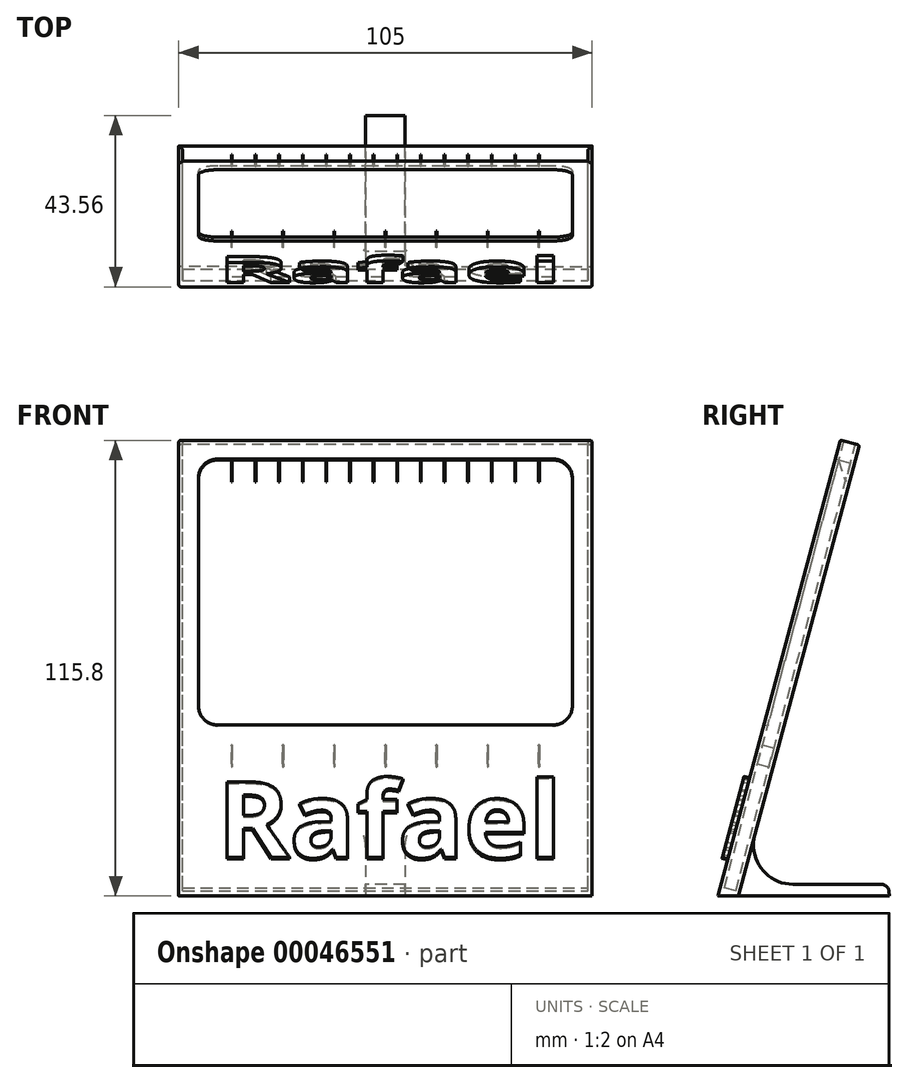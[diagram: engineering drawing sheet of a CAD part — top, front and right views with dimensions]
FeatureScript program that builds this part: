
annotation { "Feature Type Name" : "Feature", "Feature Type Description" : "" }
export const myFeature = defineFeature(function(context is Context, id is Id, definition is map)
    precondition{}
    {
        {
            var Q0;
            Q0=qCreatedBy(makeId("Right.planeOp"),FACE);
            var sketch = newSketch(context, id + "F0", { "sketchPlane" : qUnion([Q0])});
            skLineSegment(sketch, "E0", {"start": v(-21.78, 0) * mm, "end": v(9.28, 115.91) * mm});
            skLineSegment(sketch, "E1", {"start": v(9.28, 115.91) * mm, "end": v(14.1, 114.62) * mm});
            skLineSegment(sketch, "E2", {"start": v(14.1, 114.62) * mm, "end": v(-12.43, 15.59) * mm});
            skLineSegment(sketch, "E3", {"start": v(-2.77, 3) * mm, "end": v(19.68, 3) * mm});
            skLineSegment(sketch, "E4", {"start": v(21.68, 1.17) * mm, "end": v(21.78, 0) * mm});
            skLineSegment(sketch, "E5", {"start": v(21.78, 0) * mm, "end": v(-21.78, 0) * mm});
            skPoint(sketch, "E6.visualSharp", {"position": v(-15.8, 3) * mm});
            skArc(sketch, "E6.filletArc", {"start": v(-12.43, 15.59) * mm, "mid": v(-10.7, 6.91) * mm, "end": v(-2.77, 3) * mm});
            skLineSegment(sketch, "E7", {"start": v(21.52, 3) * mm, "end": v(11.7, 115.26) * mm, "construction": true});
            skPoint(sketch, "E7.endSnap0", {"position": v(11.7, 115.26) * mm});
            skPoint(sketch, "E8.visualSharp", {"position": v(21.52, 3) * mm});
            skArc(sketch, "E8.filletArc", {"start": v(21.68, 1.17) * mm, "mid": v(21.03, 2.47) * mm, "end": v(19.68, 3) * mm});
            skSolve(sketch);
        }
        {
            var Q0;
            Q0=makeQuery(id+"F0.imprint","IMPRINT",FACE,{"disambiguationData":[TD([[makeQuery(id+"F0.imprint","IMPRINT",EDGE,{"derivedFrom":sQuery(id+"F0.wireOp",EDGE,"E0")}),-1.0]])]});
            extrude(context, id + "F1", {"entities" : qUnion([Q0]), "depth" : 105 * mm});
        }
        {
            var Q0;
            Q0=makeQuery(id+"F1.opExtrude","SWEPT_FACE",FACE,{"disambiguationData":[OSD([sQuery(id+"F0.wireOp",EDGE,"E0")])]});
            var sketch = newSketch(context, id + "F2", { "sketchPlane" : qUnion([Q0])});
            skLineSegment(sketch, "E9.bottom", {"start": v(10, 109.36) * mm, "end": v(95, 109.36) * mm});
            skLineSegment(sketch, "E9.top", {"start": v(10, 39.36) * mm, "end": v(95, 39.36) * mm});
            skLineSegment(sketch, "E9.left", {"start": v(5, 104.36) * mm, "end": v(5, 44.36) * mm});
            skLineSegment(sketch, "E9.right", {"start": v(100, 104.36) * mm, "end": v(100, 44.36) * mm});
            skLineSegment(sketch, "E10", {"start": v(0, 54.36) * mm, "end": v(5, 54.36) * mm, "construction": true});
            skLineSegment(sketch, "E11", {"start": v(105, 54.36) * mm, "end": v(100, 54.36) * mm, "construction": true});
            skLineSegment(sketch, "E12", {"start": v(52.5, 109.36) * mm, "end": v(52.5, 114.36) * mm, "construction": true});
            skPoint(sketch, "E13.visualSharp", {"position": v(5, 109.36) * mm});
            skArc(sketch, "E13.filletArc", {"start": v(10, 109.36) * mm, "mid": v(6.46, 107.9) * mm, "end": v(5, 104.36) * mm});
            skPoint(sketch, "E14.visualSharp", {"position": v(100, 109.36) * mm});
            skArc(sketch, "E14.filletArc", {"start": v(100, 104.36) * mm, "mid": v(98.54, 107.9) * mm, "end": v(95, 109.36) * mm});
            skPoint(sketch, "E15.visualSharp", {"position": v(100, 39.36) * mm});
            skArc(sketch, "E15.filletArc", {"start": v(95, 39.36) * mm, "mid": v(98.54, 40.83) * mm, "end": v(100, 44.36) * mm});
            skPoint(sketch, "E16.visualSharp", {"position": v(5, 39.36) * mm});
            skArc(sketch, "E16.filletArc", {"start": v(5, 44.36) * mm, "mid": v(6.46, 40.83) * mm, "end": v(10, 39.36) * mm});
            skSolve(sketch);
        }
        {
            var Q0;
            Q0 = qSketchRegion(id + "F2", true);
            extrude(context, id + "F3", {"entities" : qUnion([Q0]), "operationType" : NewBodyOperationType.REMOVE, "oppositeDirection" : true, "depth" : 3.5 * mm});
        }
        {
            var Q0;
            Q0=makeQuery(id+"F1.opExtrude","SWEPT_FACE",FACE,{"disambiguationData":[OSD([sQuery(id+"F0.wireOp",EDGE,"E1")])]});
            var sketch = newSketch(context, id + "F4", { "sketchPlane" : qUnion([Q0])});
            skLineSegment(sketch, "E17.bottom", {"start": v(1, -17.04) * mm, "end": v(104, -17.04) * mm});
            skLineSegment(sketch, "E17.top", {"start": v(1, -20.04) * mm, "end": v(104, -20.04) * mm});
            skLineSegment(sketch, "E17.left", {"start": v(1, -17.04) * mm, "end": v(1, -20.04) * mm});
            skLineSegment(sketch, "E17.right", {"start": v(104, -17.04) * mm, "end": v(104, -20.04) * mm});
            skLineSegment(sketch, "E18", {"start": v(52.5, -21.04) * mm, "end": v(52.5, -20.04) * mm, "construction": true});
            skSolve(sketch);
        }
        {
            var Q0;
            Q0 = qSketchRegion(id + "F4", true);
            var Q1;
            Q1=makeQuery(id+"F1.opExtrude","SWEPT_FACE",FACE,{"disambiguationData":[OSD([sQuery(id+"F0.wireOp",EDGE,"E5")])]});
            extrude(context, id + "F5", {"entities" : qUnion([Q0]), "operationType" : NewBodyOperationType.REMOVE, "oppositeDirection" : true, "endBoundEntityFace" : qUnion([Q1]), "depth" : 117.5 * mm});
        }
        {
            var Q0;
            Q0=makeQuery(id+"F1.opExtrude","SWEPT_FACE",FACE,{"disambiguationData":[OSD([sQuery(id+"F0.wireOp",EDGE,"E0")])]});
            var sketch = newSketch(context, id + "F6", { "sketchPlane" : qUnion([Q0])});
            skText(sketch, "E19", { "text": "Rafael", "fontName": "OpenSans-Bold.ttf"});
            skLineSegment(sketch, "E20", {"start": v(52.5, 26.86) * mm, "end": v(52.5, 39.36) * mm, "construction": true});
            skLineSegment(sketch, "E21", {"start": v(52.5, 6.86) * mm, "end": v(52.5, -5.64) * mm, "construction": true});
            const initialGuessF6  = {"E19": [0.00982, 0.00417, 1, 0, 0.02]};
            skSetInitialGuess(sketch, initialGuessF6);
            skSolve(sketch);
        }
        {
            var Q0;
            Q0 = qSketchRegion(id + "F6", true);
            extrude(context, id + "F7", {"entities" : qUnion([Q0]), "operationType" : NewBodyOperationType.ADD, "depth" : 1.5 * mm});
        }
        {
            var Q0;
            Q0=makeQuery(id+"F1.opExtrude","CAP_FACE",FACE,{"disambiguationData":[OSD([sQuery(id+"F0.wireOp",EDGE,"E0"),sQuery(id+"F0.wireOp",EDGE,"E1"),sQuery(id+"F0.wireOp",EDGE,"E2"),sQuery(id+"F0.wireOp",EDGE,"E3"),sQuery(id+"F0.wireOp",EDGE,"E4"),sQuery(id+"F0.wireOp",EDGE,"E5"),sQuery(id+"F0.wireOp",EDGE,"E6.filletArc"),sQuery(id+"F0.wireOp",EDGE,"E8.filletArc")])],"isStart":false});
            var sketch = newSketch(context, id + "F8", { "sketchPlane" : qUnion([Q0])});
            skLineSegment(sketch, "E22", {"start": v(-12.43, 15.59) * mm, "end": v(-16.6, 0) * mm});
            skLineSegment(sketch, "E23", {"start": v(-16.6, 0) * mm, "end": v(21.78, 0) * mm});
            skArc(sketch, "E24.0", {"start": v(-12.43, 15.59) * mm, "mid": v(-10.7, 6.91) * mm, "end": v(-2.77, 3) * mm});
            skLineSegment(sketch, "E25.0", {"start": v(-2.77, 3) * mm, "end": v(19.68, 3) * mm});
            skArc(sketch, "E26.0", {"start": v(21.68, 1.17) * mm, "mid": v(21.03, 2.47) * mm, "end": v(19.68, 3) * mm});
            skLineSegment(sketch, "E27.0", {"start": v(21.68, 1.17) * mm, "end": v(21.78, 0) * mm});
            skSolve(sketch);
        }
        {
            var Q0;
            Q0 = qSketchRegion(id + "F8", true);
            extrude(context, id + "F9", {"entities" : qUnion([Q0]), "operationType" : NewBodyOperationType.REMOVE, "oppositeDirection" : true, "depth" : 47.5 * mm});
        }
        {
            var Q0;
            Q0=makeQuery(id+"F1.opExtrude","CAP_FACE",FACE,{"disambiguationData":[OSD([sQuery(id+"F0.wireOp",EDGE,"E0"),sQuery(id+"F0.wireOp",EDGE,"E1"),sQuery(id+"F0.wireOp",EDGE,"E2"),sQuery(id+"F0.wireOp",EDGE,"E3"),sQuery(id+"F0.wireOp",EDGE,"E4"),sQuery(id+"F0.wireOp",EDGE,"E5"),sQuery(id+"F0.wireOp",EDGE,"E6.filletArc"),sQuery(id+"F0.wireOp",EDGE,"E8.filletArc")])],"isStart":true});
            var sketch = newSketch(context, id + "F10", { "sketchPlane" : qUnion([Q0])});
            skLineSegment(sketch, "E28", {"start": v(12.43, 15.59) * mm, "end": v(16.6, 0) * mm});
            skLineSegment(sketch, "E29", {"start": v(16.6, 0) * mm, "end": v(-21.78, 0) * mm});
            skArc(sketch, "E30.0", {"start": v(12.43, 15.59) * mm, "mid": v(10.7, 6.91) * mm, "end": v(2.77, 3) * mm});
            skLineSegment(sketch, "E31.0", {"start": v(2.77, 3) * mm, "end": v(-19.68, 3) * mm});
            skArc(sketch, "E32.0", {"start": v(-21.68, 1.17) * mm, "mid": v(-21.03, 2.47) * mm, "end": v(-19.68, 3) * mm});
            skLineSegment(sketch, "E33.0", {"start": v(-21.68, 1.17) * mm, "end": v(-21.78, 0) * mm});
            skSolve(sketch);
        }
        {
            var Q0;
            Q0 = qSketchRegion(id + "F10", true);
            extrude(context, id + "F11", {"entities" : qUnion([Q0]), "operationType" : NewBodyOperationType.REMOVE, "oppositeDirection" : true, "depth" : 47.5 * mm});
        }
        {
            var Q0;
            Q0=makeQuery(id+"F1.opExtrude","CAP_EDGE",EDGE,{"disambiguationData":[OSD([sQuery(id+"F0.wireOp",EDGE,"E0")])],"isStart":false});
            var Q1;
            Q1=makeQuery(id+"F1.opExtrude","CAP_EDGE",EDGE,{"disambiguationData":[OSD([sQuery(id+"F0.wireOp",EDGE,"E2")])],"isStart":false});
            var Q2;
            Q2=makeQuery(id+"F1.opExtrude","CAP_EDGE",EDGE,{"disambiguationData":[OSD([sQuery(id+"F0.wireOp",EDGE,"E6.filletArc")])],"isStart":false});
            var Q3;
            Q3=makeQuery(id+"F1.opExtrude","CAP_EDGE",EDGE,{"disambiguationData":[OSD([sQuery(id+"F0.wireOp",EDGE,"E2")])],"isStart":true});
            var Q4;
            Q4=makeQuery(id+"F1.opExtrude","CAP_EDGE",EDGE,{"disambiguationData":[OSD([sQuery(id+"F0.wireOp",EDGE,"E0")])],"isStart":true});
            var Q5;
            Q5=makeQuery(id+"F1.opExtrude","SWEPT_FACE",FACE,{"disambiguationData":[OSD([sQuery(id+"F0.wireOp",EDGE,"E1")])]});
            var Q6;
            Q6=makeQuery(id+"F3.boolean.opBoolean","COPY",EDGE,{"derivedFrom":makeQuery(id+"F3.opExtrude","CAP_EDGE",EDGE,{"disambiguationData":[OSD([sQuery(id+"F2.wireOp",EDGE,"E9.top")])],"isStart":true})});
            var Q7;
            Q7=makeQuery(id+"F3.boolean.opBoolean","COPY",EDGE,{"derivedFrom":makeQuery(id+"F3.opExtrude","CAP_EDGE",EDGE,{"disambiguationData":[OSD([sQuery(id+"F2.wireOp",EDGE,"E16.filletArc")])],"isStart":true})});
            var Q8;
            Q8=makeQuery(id+"F3.boolean.opBoolean","COPY",EDGE,{"derivedFrom":makeQuery(id+"F3.opExtrude","CAP_EDGE",EDGE,{"disambiguationData":[OSD([sQuery(id+"F2.wireOp",EDGE,"E9.left")])],"isStart":true})});
            var Q9;
            Q9=makeQuery(id+"F11.boolean.opBoolean","COPY",EDGE,{"derivedFrom":makeQuery(id+"F11.opExtrude","CAP_EDGE",EDGE,{"disambiguationData":[OSD([sQuery(id+"F10.wireOp",EDGE,"E28")])],"isStart":false})});
            var Q10;
            Q10=makeQuery(id+"F11.boolean.opBoolean","COPY",EDGE,{"derivedFrom":makeQuery(id+"F11.opExtrude","CAP_EDGE",EDGE,{"disambiguationData":[OSD([sQuery(id+"F10.wireOp",EDGE,"E30.0")])],"isStart":false})});
            var Q11;
            Q11=makeQuery(id+"F9.boolean.opBoolean","COPY",EDGE,{"derivedFrom":makeQuery(id+"F9.opExtrude","CAP_EDGE",EDGE,{"disambiguationData":[OSD([sQuery(id+"F8.wireOp",EDGE,"E22")])],"isStart":false})});
            var Q12;
            Q12=makeQuery(id+"F9.boolean.opBoolean","COPY",EDGE,{"derivedFrom":makeQuery(id+"F9.opExtrude","CAP_EDGE",EDGE,{"disambiguationData":[OSD([sQuery(id+"F8.wireOp",EDGE,"E24.0")])],"isStart":false})});
            fillet(context, id + "F12", {"entities" : qUnion([Q0, Q1, Q2, Q3, Q4, Q5, Q6, Q7, Q8, Q9, Q10, Q11, Q12]), "radius" : .5 * mm, "tangentPropagation" : true, "allowEdgeOverflow" : false});
        }
        {
            var Q0;
            Q0=makeQuery(id+"F5.boolean.opBoolean","COPY",FACE,{"derivedFrom":makeQuery(id+"F5.opExtrude","SWEPT_FACE",FACE,{"disambiguationData":[OSD([sQuery(id+"F4.wireOp",EDGE,"E17.bottom")])]})});
            var sketch = newSketch(context, id + "F13", { "sketchPlane" : qUnion([Q0])});
            skLineSegment(sketch, "E34.bottom", {"start": v(13.4, 109.36) * mm, "end": v(13.6, 109.36) * mm});
            skLineSegment(sketch, "E34.top", {"start": v(13.4, 104.36) * mm, "end": v(13.6, 104.36) * mm});
            skLineSegment(sketch, "E34.left", {"start": v(13.4, 109.36) * mm, "end": v(13.4, 104.36) * mm});
            skLineSegment(sketch, "E34.right", {"start": v(13.6, 109.36) * mm, "end": v(13.6, 104.36) * mm});
            skLineSegment(sketch, "E35.1.0.0", {"start": v(19.4, 109.36) * mm, "end": v(19.4, 104.36) * mm});
            skLineSegment(sketch, "E35.1.0.1", {"start": v(19.6, 109.36) * mm, "end": v(19.6, 104.36) * mm});
            skLineSegment(sketch, "E35.1.0.2", {"start": v(19.4, 104.36) * mm, "end": v(19.6, 104.36) * mm});
            skLineSegment(sketch, "E35.1.0.3", {"start": v(19.4, 109.36) * mm, "end": v(19.6, 109.36) * mm});
            skLineSegment(sketch, "E35.2.0.0", {"start": v(25.4, 109.36) * mm, "end": v(25.4, 104.36) * mm});
            skLineSegment(sketch, "E35.2.0.1", {"start": v(25.6, 109.36) * mm, "end": v(25.6, 104.36) * mm});
            skLineSegment(sketch, "E35.2.0.2", {"start": v(25.4, 104.36) * mm, "end": v(25.6, 104.36) * mm});
            skLineSegment(sketch, "E35.2.0.3", {"start": v(25.4, 109.36) * mm, "end": v(25.6, 109.36) * mm});
            skLineSegment(sketch, "E35.3.0.0", {"start": v(31.4, 109.36) * mm, "end": v(31.4, 104.36) * mm});
            skLineSegment(sketch, "E35.3.0.1", {"start": v(31.6, 109.36) * mm, "end": v(31.6, 104.36) * mm});
            skLineSegment(sketch, "E35.3.0.2", {"start": v(31.4, 104.36) * mm, "end": v(31.6, 104.36) * mm});
            skLineSegment(sketch, "E35.3.0.3", {"start": v(31.4, 109.36) * mm, "end": v(31.6, 109.36) * mm});
            skLineSegment(sketch, "E35.4.0.0", {"start": v(37.4, 109.36) * mm, "end": v(37.4, 104.36) * mm});
            skLineSegment(sketch, "E35.4.0.1", {"start": v(37.6, 109.36) * mm, "end": v(37.6, 104.36) * mm});
            skLineSegment(sketch, "E35.4.0.2", {"start": v(37.4, 104.36) * mm, "end": v(37.6, 104.36) * mm});
            skLineSegment(sketch, "E35.4.0.3", {"start": v(37.4, 109.36) * mm, "end": v(37.6, 109.36) * mm});
            skLineSegment(sketch, "E35.5.0.0", {"start": v(43.4, 109.36) * mm, "end": v(43.4, 104.36) * mm});
            skLineSegment(sketch, "E35.5.0.1", {"start": v(43.6, 109.36) * mm, "end": v(43.6, 104.36) * mm});
            skLineSegment(sketch, "E35.5.0.2", {"start": v(43.4, 104.36) * mm, "end": v(43.6, 104.36) * mm});
            skLineSegment(sketch, "E35.5.0.3", {"start": v(43.4, 109.36) * mm, "end": v(43.6, 109.36) * mm});
            skLineSegment(sketch, "E35.6.0.0", {"start": v(49.4, 109.36) * mm, "end": v(49.4, 104.36) * mm});
            skLineSegment(sketch, "E35.6.0.1", {"start": v(49.6, 109.36) * mm, "end": v(49.6, 104.36) * mm});
            skLineSegment(sketch, "E35.6.0.2", {"start": v(49.4, 104.36) * mm, "end": v(49.6, 104.36) * mm});
            skLineSegment(sketch, "E35.6.0.3", {"start": v(49.4, 109.36) * mm, "end": v(49.6, 109.36) * mm});
            skLineSegment(sketch, "E35.7.0.0", {"start": v(55.4, 109.36) * mm, "end": v(55.4, 104.36) * mm});
            skLineSegment(sketch, "E35.7.0.1", {"start": v(55.6, 109.36) * mm, "end": v(55.6, 104.36) * mm});
            skLineSegment(sketch, "E35.7.0.2", {"start": v(55.4, 104.36) * mm, "end": v(55.6, 104.36) * mm});
            skLineSegment(sketch, "E35.7.0.3", {"start": v(55.4, 109.36) * mm, "end": v(55.6, 109.36) * mm});
            skLineSegment(sketch, "E35.8.0.0", {"start": v(61.4, 109.36) * mm, "end": v(61.4, 104.36) * mm});
            skLineSegment(sketch, "E35.8.0.1", {"start": v(61.6, 109.36) * mm, "end": v(61.6, 104.36) * mm});
            skLineSegment(sketch, "E35.8.0.2", {"start": v(61.4, 104.36) * mm, "end": v(61.6, 104.36) * mm});
            skLineSegment(sketch, "E35.8.0.3", {"start": v(61.4, 109.36) * mm, "end": v(61.6, 109.36) * mm});
            skLineSegment(sketch, "E35.9.0.0", {"start": v(67.4, 109.36) * mm, "end": v(67.4, 104.36) * mm});
            skLineSegment(sketch, "E35.9.0.1", {"start": v(67.6, 109.36) * mm, "end": v(67.6, 104.36) * mm});
            skLineSegment(sketch, "E35.9.0.2", {"start": v(67.4, 104.36) * mm, "end": v(67.6, 104.36) * mm});
            skLineSegment(sketch, "E35.9.0.3", {"start": v(67.4, 109.36) * mm, "end": v(67.6, 109.36) * mm});
            skLineSegment(sketch, "E35.direction1", {"start": v(13.4, 104.36) * mm, "end": v(19.4, 104.36) * mm, "construction": true});
            skLineSegment(sketch, "E36.0.10.0", {"start": v(73.4, 109.36) * mm, "end": v(73.4, 104.36) * mm});
            skLineSegment(sketch, "E36.3.10.0", {"start": v(73.6, 109.36) * mm, "end": v(73.6, 104.36) * mm});
            skLineSegment(sketch, "E36.6.10.0", {"start": v(73.4, 104.36) * mm, "end": v(73.6, 104.36) * mm});
            skLineSegment(sketch, "E36.9.10.0", {"start": v(73.4, 109.36) * mm, "end": v(73.6, 109.36) * mm});
            skLineSegment(sketch, "E37.0.11.0", {"start": v(79.4, 109.36) * mm, "end": v(79.4, 104.36) * mm});
            skLineSegment(sketch, "E37.3.11.0", {"start": v(79.6, 109.36) * mm, "end": v(79.6, 104.36) * mm});
            skLineSegment(sketch, "E37.6.11.0", {"start": v(79.4, 104.36) * mm, "end": v(79.6, 104.36) * mm});
            skLineSegment(sketch, "E37.9.11.0", {"start": v(79.4, 109.36) * mm, "end": v(79.6, 109.36) * mm});
            skLineSegment(sketch, "E38.0.12.0", {"start": v(85.4, 109.36) * mm, "end": v(85.4, 104.36) * mm});
            skLineSegment(sketch, "E38.3.12.0", {"start": v(85.6, 109.36) * mm, "end": v(85.6, 104.36) * mm});
            skLineSegment(sketch, "E38.6.12.0", {"start": v(85.4, 104.36) * mm, "end": v(85.6, 104.36) * mm});
            skLineSegment(sketch, "E38.9.12.0", {"start": v(85.4, 109.36) * mm, "end": v(85.6, 109.36) * mm});
            skLineSegment(sketch, "E39.0.13.0", {"start": v(91.4, 109.36) * mm, "end": v(91.4, 104.36) * mm});
            skLineSegment(sketch, "E39.3.13.0", {"start": v(91.6, 109.36) * mm, "end": v(91.6, 104.36) * mm});
            skLineSegment(sketch, "E39.6.13.0", {"start": v(91.4, 104.36) * mm, "end": v(91.6, 104.36) * mm});
            skLineSegment(sketch, "E39.9.13.0", {"start": v(91.4, 109.36) * mm, "end": v(91.6, 109.36) * mm});
            skSolve(sketch);
        }
        {
            var Q0;
            Q0 = qSketchRegion(id + "F13", true);
            var Q1;
            {var subQ0=sQuery(id+"F0.wireOp",EDGE,"E0");var subQ1=sQuery(id+"F0.wireOp",EDGE,"E1");Q1=makeQuery(id+"F7.boolean.opBoolean","SPLIT",FACE,{"disambiguationData":[TD([makeQuery(id+"F1.opExtrude","SWEPT_FACE",FACE,{"disambiguationData":[OSD([subQ1])]})])],"derivedFrom":makeQuery(id+"F1.opExtrude","SWEPT_FACE",FACE,{"disambiguationData":[OSD([subQ0])]})});}
            var Q2;
            Q2=makeQuery(id+"F1.opExtrude","SWEPT_BODY",BODY,{"disambiguationData":[OSD([sQuery(id+"F0.wireOp",EDGE,"E0"),sQuery(id+"F0.wireOp",EDGE,"E1"),sQuery(id+"F0.wireOp",EDGE,"E2"),sQuery(id+"F0.wireOp",EDGE,"E3"),sQuery(id+"F0.wireOp",EDGE,"E4"),sQuery(id+"F0.wireOp",EDGE,"E5"),sQuery(id+"F0.wireOp",EDGE,"E6.filletArc"),sQuery(id+"F0.wireOp",EDGE,"E8.filletArc")])]});
            extrude(context, id + "F14", {"entities" : qUnion([Q0]), "operationType" : NewBodyOperationType.ADD, "endBoundEntityFace" : qUnion([Q1]), "endBoundEntityBody" : qUnion([Q2]), "depth" : 3.1 * mm});
        }
        {
            var Q0;
            Q0=makeQuery(id+"F14.opExtrude","SWEPT_FACE",FACE,{"disambiguationData":[OSD([sQuery(id+"F13.wireOp",EDGE,"E34.left")])]});
            var sketch = newSketch(context, id + "F15", { "sketchPlane" : qUnion([Q0])});
            skLineSegment(sketch, "E40", {"start": v(-10.56, 105.22) * mm, "end": v(-7.56, 106.02) * mm});
            skLineSegment(sketch, "E41", {"start": v(-7.56, 106.02) * mm, "end": v(-8.85, 110.85) * mm});
            skLineSegment(sketch, "E42", {"start": v(-8.85, 110.85) * mm, "end": v(-10.56, 105.22) * mm});
            skSolve(sketch);
        }
        {
            var Q0;
            Q0 = qSketchRegion(id + "F15", true);
            var Q1;
            Q1=makeQuery(id+"F14.opExtrude","SWEPT_FACE",FACE,{"disambiguationData":[OSD([sQuery(id+"F13.wireOp",EDGE,"E39.3.13.0")])]});
            extrude(context, id + "F16", {"entities" : qUnion([Q0]), "operationType" : NewBodyOperationType.REMOVE, "endBound" : BoundingType.UP_TO_SURFACE, "oppositeDirection" : true, "endBoundEntityFace" : qUnion([Q1]), "depth" : 25 * mm});
        }
        {
            var Q0;
            Q0=makeQuery(id+"F5.boolean.opBoolean","COPY",FACE,{"derivedFrom":makeQuery(id+"F5.opExtrude","SWEPT_FACE",FACE,{"disambiguationData":[OSD([sQuery(id+"F4.wireOp",EDGE,"E17.bottom")])]})});
            var sketch = newSketch(context, id + "F17", { "sketchPlane" : qUnion([Q0])});
            skLineSegment(sketch, "E43.bottom", {"start": v(13.4, 34.36) * mm, "end": v(13.6, 34.36) * mm});
            skLineSegment(sketch, "E43.top", {"start": v(13.4, 29.36) * mm, "end": v(13.6, 29.36) * mm});
            skLineSegment(sketch, "E43.left", {"start": v(13.4, 34.36) * mm, "end": v(13.4, 29.36) * mm});
            skLineSegment(sketch, "E43.right", {"start": v(13.6, 34.36) * mm, "end": v(13.6, 29.36) * mm});
            skLineSegment(sketch, "E44.1.0.0", {"start": v(26.4, 34.36) * mm, "end": v(26.4, 29.36) * mm});
            skLineSegment(sketch, "E44.1.0.1", {"start": v(26.6, 34.36) * mm, "end": v(26.6, 29.36) * mm});
            skLineSegment(sketch, "E44.1.0.2", {"start": v(26.4, 29.36) * mm, "end": v(26.6, 29.36) * mm});
            skLineSegment(sketch, "E44.1.0.3", {"start": v(26.4, 34.36) * mm, "end": v(26.6, 34.36) * mm});
            skLineSegment(sketch, "E44.2.0.0", {"start": v(39.4, 34.36) * mm, "end": v(39.4, 29.36) * mm});
            skLineSegment(sketch, "E44.2.0.1", {"start": v(39.6, 34.36) * mm, "end": v(39.6, 29.36) * mm});
            skLineSegment(sketch, "E44.2.0.2", {"start": v(39.4, 29.36) * mm, "end": v(39.6, 29.36) * mm});
            skLineSegment(sketch, "E44.2.0.3", {"start": v(39.4, 34.36) * mm, "end": v(39.6, 34.36) * mm});
            skLineSegment(sketch, "E44.3.0.0", {"start": v(52.4, 34.36) * mm, "end": v(52.4, 29.36) * mm});
            skLineSegment(sketch, "E44.3.0.1", {"start": v(52.6, 34.36) * mm, "end": v(52.6, 29.36) * mm});
            skLineSegment(sketch, "E44.3.0.2", {"start": v(52.4, 29.36) * mm, "end": v(52.6, 29.36) * mm});
            skLineSegment(sketch, "E44.3.0.3", {"start": v(52.4, 34.36) * mm, "end": v(52.6, 34.36) * mm});
            skLineSegment(sketch, "E44.4.0.0", {"start": v(65.4, 34.36) * mm, "end": v(65.4, 29.36) * mm});
            skLineSegment(sketch, "E44.4.0.1", {"start": v(65.6, 34.36) * mm, "end": v(65.6, 29.36) * mm});
            skLineSegment(sketch, "E44.4.0.2", {"start": v(65.4, 29.36) * mm, "end": v(65.6, 29.36) * mm});
            skLineSegment(sketch, "E44.4.0.3", {"start": v(65.4, 34.36) * mm, "end": v(65.6, 34.36) * mm});
            skLineSegment(sketch, "E44.5.0.0", {"start": v(78.4, 34.36) * mm, "end": v(78.4, 29.36) * mm});
            skLineSegment(sketch, "E44.5.0.1", {"start": v(78.6, 34.36) * mm, "end": v(78.6, 29.36) * mm});
            skLineSegment(sketch, "E44.5.0.2", {"start": v(78.4, 29.36) * mm, "end": v(78.6, 29.36) * mm});
            skLineSegment(sketch, "E44.5.0.3", {"start": v(78.4, 34.36) * mm, "end": v(78.6, 34.36) * mm});
            skLineSegment(sketch, "E44.6.0.0", {"start": v(91.4, 34.36) * mm, "end": v(91.4, 29.36) * mm});
            skLineSegment(sketch, "E44.6.0.1", {"start": v(91.6, 34.36) * mm, "end": v(91.6, 29.36) * mm});
            skLineSegment(sketch, "E44.6.0.2", {"start": v(91.4, 29.36) * mm, "end": v(91.6, 29.36) * mm});
            skLineSegment(sketch, "E44.6.0.3", {"start": v(91.4, 34.36) * mm, "end": v(91.6, 34.36) * mm});
            skLineSegment(sketch, "E44.direction1", {"start": v(13.4, 29.36) * mm, "end": v(26.4, 29.36) * mm, "construction": true});
            skSolve(sketch);
        }
        {
            var Q0;
            Q0 = qSketchRegion(id + "F17", true);
            var Q1;
            {var subQ6=sQuery(id+"F0.wireOp",EDGE,"E1");var subQ7=sQuery(id+"F0.wireOp",EDGE,"E0");Q1=makeQuery(id+"F7.boolean.opBoolean","SPLIT",FACE,{"disambiguationData":[TD([makeQuery(id+"F1.opExtrude","SWEPT_FACE",FACE,{"disambiguationData":[OSD([subQ6])]})])],"derivedFrom":makeQuery(id+"F1.opExtrude","SWEPT_FACE",FACE,{"disambiguationData":[OSD([subQ7])]})});}
            extrude(context, id + "F18", {"entities" : qUnion([Q0]), "operationType" : NewBodyOperationType.ADD, "endBound" : BoundingType.UP_TO_SURFACE, "endBoundEntityFace" : qUnion([Q1]), "depth" : 25 * mm});
        }
    });
